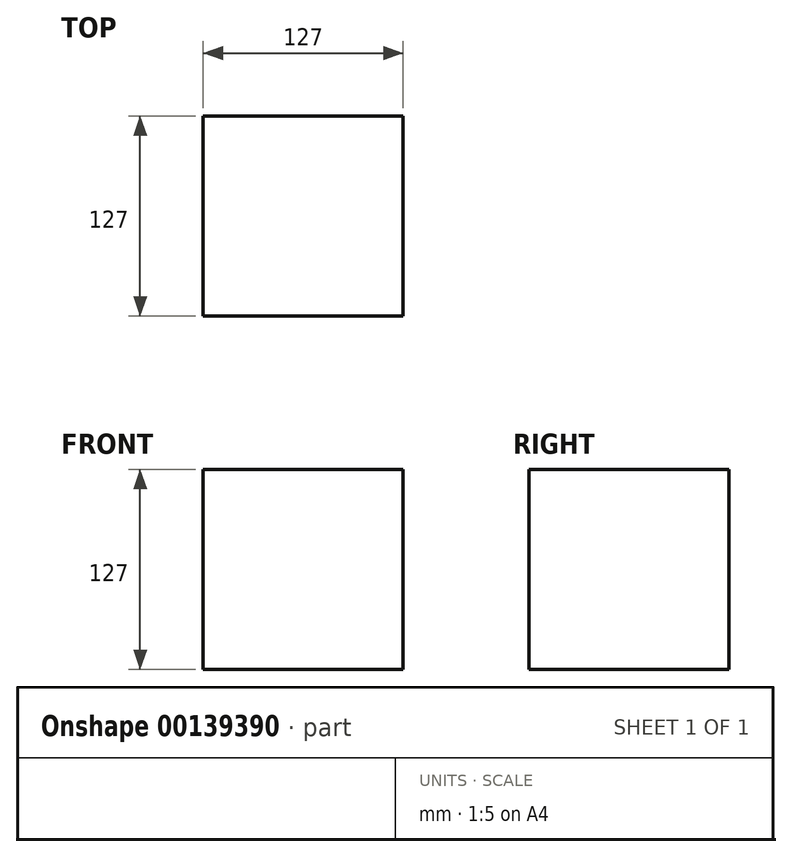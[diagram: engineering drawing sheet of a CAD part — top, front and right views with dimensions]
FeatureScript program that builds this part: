
annotation { "Feature Type Name" : "Feature", "Feature Type Description" : "" }
export const myFeature = defineFeature(function(context is Context, id is Id, definition is map)
    precondition{}
    {
        {
            var Q0;
            Q0=qCreatedBy(makeId("Top.planeOp"),FACE);
            var sketch = newSketch(context, id + "F0", { "sketchPlane" : qUnion([Q0])});
            skLineSegment(sketch, "E0.bottom", {"start": v(-63.5, 63.5) * mm, "end": v(63.5, 63.5) * mm});
            skLineSegment(sketch, "E0.top", {"start": v(-63.5, -63.5) * mm, "end": v(63.5, -63.5) * mm});
            skLineSegment(sketch, "E0.left", {"start": v(-63.5, 63.5) * mm, "end": v(-63.5, -63.5) * mm});
            skLineSegment(sketch, "E0.right", {"start": v(63.5, 63.5) * mm, "end": v(63.5, -63.5) * mm});
            skSolve(sketch);
        }
        {
            var Q0;
            Q0=makeQuery(id+"F0.imprint","IMPRINT",FACE,{"disambiguationData":[TD([[makeQuery(id+"F0.imprint","IMPRINT",EDGE,{"derivedFrom":sQuery(id+"F0.wireOp",EDGE,"E0.bottom")}),-1.0]])]});
            extrude(context, id + "F1", {"entities" : qUnion([Q0]), "endBound" : BoundingType.SYMMETRIC, "depth" : 127 * mm});
        }
    });
